# Revit family: 1_天吊埋込タイプ 標準 単相100V_3相200V-60
name_source: partatom
category: 機械設備
units: mm (PartAtom-declared; Revit-internal decimal feet)

## family parameters
OmniClass タイトル = Centrifugal Fans
OmniClass 番号 = 23.75.35.17.27
パーツ タイプ = 割り込み
ロード時にボイドで切り取り = いいえ
丸型コネクタ寸法 = 直径を使用
作業面ベース = いいえ
共有 = いいえ
常に垂直 = はい
部屋計算ポイント = はい

## types (18) — shared parameters
Clearance Left = 450  [stored 1.47638 ft]
IfcExportAs = IfcFanType
IfcExportType = CENTRIFUGALFORWARDCURVED
MID静圧 = 0.0 Pa
MID風量 = 0.0 m³/h
OmniClassCode = 23-33 31 19 13 15
URL = https://www.mitsubishielectric.co.jp
Uniclass2015Code = Pr_65_67_29_12
Uniclass2015Title = Centrifugal fans
Uniclass2015Version = Systems v1.9
サービススペース = はい
ファンの種類 = 多翼形
仕様書バージョン = Version1.0
企業コード = 108420
分類コード = 50052502100020
周波数 = 60 Hz
呼称 = 消音ボックス付送風機
実風量 = 0.0 m³/h
本体マテリアル = 溶融亜鉛めっき鋼板
極 = 4
法定耐用年数 = 15
盤工事区分 = 電気工事
積算_科目 = 2 換気設備
製品出荷対象 = 国内
製造元 = 三菱電機株式会社
設置方法 = 天吊
説明 = ストレートシロッコファン天吊埋込タイプ（標準形）
負荷分類 = 3_ファン類
運転質量 = 0.00 kg
zero-valued in all types: Clearance Back, Clearance Bottom, Clearance Front, Clearance Right, Clearance Top

## per-type parameters (varying)
- BFS-15SG: Depth=335  [stored 1.09908 ft]; Height=225  [stored 0.738189 ft]; M=100  [stored 0.328084 ft]; MAX静圧=39.0 Pa; MAX風量=150.0 m³/h; MIN静圧=26.0 Pa; MIN風量=96.0 m³/h; Width=223  [stored 0.731627 ft]; ダクト径=100 mm; 価格=30900 $; 天吊金具ピッチ奥行=300; 天吊金具ピッチ幅=299; 形名=BFS-SG : BFS-15SG; 極数=2; 消費電力=24 W; 番手=#1; 相=1; 製品リリース年月=2018年4月23日; 製品質量=6.00 kg; 質量=7.20 kg; 電動機出力=8 W; 電圧=100 V; 騒音レベル(dB(A))=34; 騒音レベル(dB(A))_側面=20; 騒音レベル(dB(A))_吐出=34; 騒音レベル(dB(A))_吸込=30
- BFS-30SG: Depth=335  [stored 1.09908 ft]; Height=225  [stored 0.738189 ft]; M=100  [stored 0.328084 ft]; MAX静圧=39.0 Pa; MAX風量=300.0 m³/h; MIN静圧=15.0 Pa; MIN風量=182.0 m³/h; Width=223  [stored 0.731627 ft]; ダクト径=150 mm; 価格=44700 $; 天吊金具ピッチ奥行=300; 天吊金具ピッチ幅=299; 形名=BFS-SG : BFS-30SG; 極数=2; 消費電力=44 W; 番手=#1; 相=1; 製品リリース年月=2018年4月23日; 製品質量=6.00 kg; 質量=7.20 kg; 電動機出力=16 W; 電圧=100 V; 騒音レベル(dB(A))=40; 騒音レベル(dB(A))_側面=23.5; 騒音レベル(dB(A))_吐出=40; 騒音レベル(dB(A))_吸込=36
- BFS-40SG: Depth=388  [stored 1.27297 ft]; Height=255  [stored 0.836614 ft]; M=100  [stored 0.328084 ft]; MAX静圧=59.0 Pa; MAX風量=400.0 m³/h; MIN静圧=30.0 Pa; MIN風量=273.0 m³/h; Width=255  [stored 0.836614 ft]; ダクト径=150 mm; 価格=52800 $; 天吊金具ピッチ奥行=353; 天吊金具ピッチ幅=331; 形名=BFS-SG : BFS-40SG; 極数=2; 消費電力=66 W; 番手=#1 1/4; 相=1; 製品リリース年月=2018年4月23日; 製品質量=8.00 kg; 質量=9.60 kg; 電動機出力=25 W; 電圧=100 V; 騒音レベル(dB(A))=44; 騒音レベル(dB(A))_側面=27; 騒音レベル(dB(A))_吐出=44; 騒音レベル(dB(A))_吸込=38
- BFS-50SG: Depth=423  [stored 1.3878 ft]; Height=255  [stored 0.836614 ft]; M=100  [stored 0.328084 ft]; MAX静圧=130.0 Pa; MAX風量=500.0 m³/h; MIN静圧=100.0 Pa; MIN風量=380.0 m³/h; Width=325  [stored 1.06627 ft]; ダクト径=200 mm; 価格=74800 $; 参照している仕様書等のバージョン=公共建築工事標準仕様書（機械設備工事編）平成31年度版; 天吊金具ピッチ奥行=388  [stored 1.27297 ft]; 天吊金具ピッチ幅=401; 形名=BFS-SG : BFS-50SG; 極数=2; 消費電力=88 W; 番手=#1 1/4; 相=1; 製品リリース年月=2018年4月23日; 製品質量=10.50 kg; 質量=12.60 kg; 電動機出力=45 W; 電圧=100 V; 騒音レベル(dB(A))=49; 騒音レベル(dB(A))_側面=25.5; 騒音レベル(dB(A))_吐出=49; 騒音レベル(dB(A))_吸込=37.5
- BFS-65SG: Depth=488  [stored 1.60105 ft]; Height=305  [stored 1.00066 ft]; M=100  [stored 0.328084 ft]; MAX静圧=118.0 Pa; MAX風量=650.0 m³/h; MIN静圧=91.0 Pa; MIN風量=498.0 m³/h; Width=373  [stored 1.22375 ft]; ダクト径=200 mm; 価格=79400 $; 参照している仕様書等のバージョン=公共建築工事標準仕様書（機械設備工事編）平成31年度版; 天吊金具ピッチ奥行=453  [stored 1.48622 ft]; 天吊金具ピッチ幅=449  [stored 1.4731 ft]; 形名=BFS-SG : BFS-65SG; 極数=2; 消費電力=126 W; 番手=#1 1/4; 相=1; 製品リリース年月=2018年4月23日; 製品質量=13.00 kg; 質量=15.60 kg; 電動機出力=65 W; 電圧=100 V; 騒音レベル(dB(A))=51; 騒音レベル(dB(A))_側面=29; 騒音レベル(dB(A))_吐出=51; 騒音レベル(dB(A))_吸込=38
- BFS-80SG: Depth=488  [stored 1.60105 ft]; Height=305  [stored 1.00066 ft]; M=100  [stored 0.328084 ft]; MAX静圧=98.0 Pa; MAX風量=800.0 m³/h; MIN静圧=88.0 Pa; MIN風量=600.0 m³/h; Width=373  [stored 1.22375 ft]; ダクト径=200 mm; 価格=83900 $; 参照している仕様書等のバージョン=公共建築工事標準仕様書（機械設備工事編）平成31年度版; 天吊金具ピッチ奥行=453  [stored 1.48622 ft]; 天吊金具ピッチ幅=449  [stored 1.4731 ft]; 形名=BFS-SG : BFS-80SG; 極数=2; 消費電力=155 W; 番手=#1 1/4; 相=1; 製品リリース年月=2018年4月23日; 製品質量=13.50 kg; 質量=16.20 kg; 電動機出力=80 W; 電圧=100 V; 騒音レベル(dB(A))=53; 騒音レベル(dB(A))_側面=30.5; 騒音レベル(dB(A))_吐出=53; 騒音レベル(dB(A))_吸込=39.5
- BFS-90SG: Depth=488  [stored 1.60105 ft]; Height=305  [stored 1.00066 ft]; M=100  [stored 0.328084 ft]; MAX静圧=128.0 Pa; MAX風量=900.0 m³/h; MIN静圧=110.0 Pa; MIN風量=684.0 m³/h; Width=393  [stored 1.28937 ft]; ダクト径=200 mm; 価格=88500 $; 参照している仕様書等のバージョン=公共建築工事標準仕様書（機械設備工事編）平成31年度版; 天吊金具ピッチ奥行=453  [stored 1.48622 ft]; 天吊金具ピッチ幅=469; 形名=BFS-SG : BFS-90SG; 極数=2; 消費電力=205 W; 番手=#1 1/2; 相=1; 製品リリース年月=2018年4月23日; 製品質量=15.50 kg; 質量=18.60 kg; 電動機出力=110 W; 電圧=100 V; 騒音レベル(dB(A))=55; 騒音レベル(dB(A))_側面=32; 騒音レベル(dB(A))_吐出=55; 騒音レベル(dB(A))_吸込=41
- BFS-100SG: Depth=488  [stored 1.60105 ft]; Height=305  [stored 1.00066 ft]; M=100  [stored 0.328084 ft]; MAX静圧=145.0 Pa; MAX風量=1000.0 m³/h; MIN静圧=187.0 Pa; MIN風量=865.0 m³/h; Width=393  [stored 1.28937 ft]; ダクト径=200 mm; 価格=93600 $; 参照している仕様書等のバージョン=公共建築工事標準仕様書（機械設備工事編）平成31年度版; 天吊金具ピッチ奥行=453  [stored 1.48622 ft]; 天吊金具ピッチ幅=469; 形名=BFS-SG : BFS-100SG; 極数=2; 消費電力=247 W; 番手=#1 1/2; 相=1; 製品リリース年月=2018年4月23日; 製品質量=16.00 kg; 質量=19.20 kg; 電動機出力=160 W; 電圧=100 V; 騒音レベル(dB(A))=58; 騒音レベル(dB(A))_側面=34.5; 騒音レベル(dB(A))_吐出=58; 騒音レベル(dB(A))_吸込=43
- BFS-120SG: Depth=590  [stored 1.9357 ft]; Height=350  [stored 1.14829 ft]; M=100  [stored 0.328084 ft]; MAX静圧=220.0 Pa; MAX風量=1200.0 m³/h; MIN静圧=195.0 Pa; MIN風量=1030.0 m³/h; Width=391; ダクト径=250 mm; 価格=102100 $; 参照している仕様書等のバージョン=公共建築工事標準仕様書（機械設備工事編）平成31年度版; 天吊金具ピッチ奥行=555  [stored 1.82087 ft]; 天吊金具ピッチ幅=467  [stored 1.53215 ft]; 形名=BFS-SG : BFS-120SG; 極数=2; 消費電力=352 W; 番手=#1 1/2; 相=1; 製品リリース年月=2018年4月23日; 製品質量=19.50 kg; 質量=23.40 kg; 電動機出力=200 W; 電圧=100 V; 騒音レベル(dB(A))=59; 騒音レベル(dB(A))_側面=34.5; 騒音レベル(dB(A))_吐出=59; 騒音レベル(dB(A))_吸込=46.5
- BFS-150SG: Depth=590  [stored 1.9357 ft]; Height=350  [stored 1.14829 ft]; M=100  [stored 0.328084 ft]; MAX静圧=180.0 Pa; MAX風量=1500.0 m³/h; MIN静圧=184.0 Pa; MIN風量=1243.0 m³/h; Width=391; ダクト径=250 mm; 価格=108200 $; 参照している仕様書等のバージョン=公共建築工事標準仕様書（機械設備工事編）平成31年度版; 天吊金具ピッチ奥行=555  [stored 1.82087 ft]; 天吊金具ピッチ幅=467  [stored 1.53215 ft]; 形名=BFS-SG : BFS-150SG; 極数=2; 消費電力=498 W; 番手=#1 1/2; 相=1; 製品リリース年月=2018年4月23日; 製品質量=19.50 kg; 質量=23.40 kg; 電動機出力=340 W; 電圧=100 V; 騒音レベル(dB(A))=63; 騒音レベル(dB(A))_側面=37.5; 騒音レベル(dB(A))_吐出=63; 騒音レベル(dB(A))_吸込=50
- BFS-180TG: Depth=645  [stored 2.11614 ft]; Height=350  [stored 1.14829 ft]; M=85  [stored 0.278871 ft]; MAX静圧=167.0 Pa; MAX風量=1800.0 m³/h; MIN静圧=0.0 Pa; MIN風量=0.0 m³/h; Width=476  [stored 1.56168 ft]; ダクト径=250 mm; 価格=123900 $; 参照している仕様書等のバージョン=公共建築工事標準仕様書（機械設備工事編）平成31年度版; 天吊金具ピッチ奥行=610  [stored 2.00131 ft]; 天吊金具ピッチ幅=552  [stored 1.81102 ft]; 形名=BFS-TG : BFS-180TG; 極数=3; 消費電力=573 W; 番手=#1 1/2; 相=3; 製品リリース年月=2018年4月23日; 製品質量=22.50 kg; 質量=27.00 kg; 電動機出力=360 W; 電圧=200 V; 騒音レベル(dB(A))=64; 騒音レベル(dB(A))_側面=38.5; 騒音レベル(dB(A))_吐出=64; 騒音レベル(dB(A))_吸込=50
- BFS-210TG: Depth=645  [stored 2.11614 ft]; Height=350  [stored 1.14829 ft]; M=100  [stored 0.328084 ft]; MAX静圧=191.0 Pa; MAX風量=2100.0 m³/h; MIN静圧=0.0 Pa; MIN風量=0.0 m³/h; Width=476  [stored 1.56168 ft]; ダクト径=300 mm; 価格=176400 $; 参照している仕様書等のバージョン=公共建築工事標準仕様書（機械設備工事編）平成31年度版; 天吊金具ピッチ奥行=610  [stored 2.00131 ft]; 天吊金具ピッチ幅=552  [stored 1.81102 ft]; 形名=BFS-TG : BFS-210TG; 極数=3; 消費電力=665 W; 番手=#1 1/2; 相=3; 製品リリース年月=2018年4月23日; 製品質量=22.50 kg; 質量=27.00 kg; 電動機出力=490 W; 電圧=200 V; 騒音レベル(dB(A))=67; 騒音レベル(dB(A))_側面=40; 騒音レベル(dB(A))_吐出=67; 騒音レベル(dB(A))_吸込=52.5
- BFS-240TA: Depth=717  [stored 2.35236 ft]; Height=373  [stored 1.22375 ft]; M=100  [stored 0.328084 ft]; MAX静圧=220.0 Pa; MAX風量=2400.0 m³/h; MIN静圧=0.0 Pa; MIN風量=0.0 m³/h; Width=493  [stored 1.61745 ft]; ダクト径=300 mm; 価格=182000 $; 参照している仕様書等のバージョン=公共建築工事標準仕様書（機械設備工事編）平成31年度版; 天吊金具ピッチ奥行=664  [stored 2.17848 ft]; 天吊金具ピッチ幅=602  [stored 1.97507 ft]; 形名=BFS-TG : BFS-240TA; 極数=3; 消費電力=810 W; 番手=#1 1/2; 相=3; 製品リリース年月=2003年4月; 製品質量=33.00 kg; 質量=39.60 kg; 電動機出力=1100 W; 電圧=200 V; 騒音レベル(dB(A))=69; 騒音レベル(dB(A))_側面=42.5; 騒音レベル(dB(A))_吐出=69; 騒音レベル(dB(A))_吸込=51.5
- BFS-80TG: Depth=488  [stored 1.60105 ft]; Height=305  [stored 1.00066 ft]; M=85  [stored 0.278871 ft]; MAX静圧=98.0 Pa; MAX風量=800.0 m³/h; MIN静圧=73.0 Pa; MIN風量=550.0 m³/h; Width=373  [stored 1.22375 ft]; ダクト径=200 mm; 価格=83900 $; 参照している仕様書等のバージョン=公共建築工事標準仕様書（機械設備工事編）平成31年度版; 天吊金具ピッチ奥行=453  [stored 1.48622 ft]; 天吊金具ピッチ幅=449  [stored 1.4731 ft]; 形名=BFS-TG : BFS-80TG; 極数=3; 消費電力=148 W; 番手=#1 1/4; 相=3; 製品リリース年月=2018年4月23日; 製品質量=15.00 kg; 質量=18.00 kg; 電動機出力=80 W; 電圧=200 V; 騒音レベル(dB(A))=53; 騒音レベル(dB(A))_側面=31.5; 騒音レベル(dB(A))_吐出=53; 騒音レベル(dB(A))_吸込=40
- BFS-90TG: Depth=488  [stored 1.60105 ft]; Height=305  [stored 1.00066 ft]; M=85  [stored 0.278871 ft]; MAX静圧=128.0 Pa; MAX風量=900.0 m³/h; MIN静圧=96.0 Pa; MIN風量=640.0 m³/h; Width=393  [stored 1.28937 ft]; ダクト径=200 mm; 価格=88500 $; 参照している仕様書等のバージョン=公共建築工事標準仕様書（機械設備工事編）平成31年度版; 天吊金具ピッチ奥行=453  [stored 1.48622 ft]; 天吊金具ピッチ幅=469; 形名=BFS-TG : BFS-90TG; 極数=3; 消費電力=194 W; 番手=#1 1/2; 相=3; 製品リリース年月=2018年4月23日; 製品質量=15.50 kg; 質量=18.60 kg; 電動機出力=100 W; 電圧=200 V; 騒音レベル(dB(A))=55; 騒音レベル(dB(A))_側面=34; 騒音レベル(dB(A))_吐出=55; 騒音レベル(dB(A))_吸込=41
- BFS-100TG: Depth=488  [stored 1.60105 ft]; Height=305  [stored 1.00066 ft]; M=85  [stored 0.278871 ft]; MAX静圧=145.0 Pa; MAX風量=1000.0 m³/h; MIN静圧=115.0 Pa; MIN風量=678.0 m³/h; Width=393  [stored 1.28937 ft]; ダクト径=200 mm; 価格=93600 $; 参照している仕様書等のバージョン=公共建築工事標準仕様書（機械設備工事編）平成31年度版; 天吊金具ピッチ奥行=453  [stored 1.48622 ft]; 天吊金具ピッチ幅=469; 形名=BFS-TG : BFS-100TG; 極数=3; 消費電力=237 W; 番手=#1 1/2; 相=3; 製品リリース年月=2018年4月23日; 製品質量=15.50 kg; 質量=18.60 kg; 電動機出力=150 W; 電圧=200 V; 騒音レベル(dB(A))=58; 騒音レベル(dB(A))_側面=34; 騒音レベル(dB(A))_吐出=58; 騒音レベル(dB(A))_吸込=43
- BFS-120TG: Depth=590  [stored 1.9357 ft]; Height=350  [stored 1.14829 ft]; M=85  [stored 0.278871 ft]; MAX静圧=220.0 Pa; MAX風量=1200.0 m³/h; MIN静圧=121.0 Pa; MIN風量=821.0 m³/h; Width=391; ダクト径=250 mm; 価格=102100 $; 参照している仕様書等のバージョン=公共建築工事標準仕様書（機械設備工事編）平成31年度版; 天吊金具ピッチ奥行=555  [stored 1.82087 ft]; 天吊金具ピッチ幅=467  [stored 1.53215 ft]; 形名=BFS-TG : BFS-120TG; 極数=3; 消費電力=342 W; 番手=#1 1/2; 相=3; 製品リリース年月=2018年4月23日; 製品質量=19.50 kg; 質量=23.40 kg; 電動機出力=180 W; 電圧=200 V; 騒音レベル(dB(A))=58; 騒音レベル(dB(A))_側面=35.5; 騒音レベル(dB(A))_吐出=58; 騒音レベル(dB(A))_吸込=46.5
- BFS-150TG: Depth=590  [stored 1.9357 ft]; Height=350  [stored 1.14829 ft]; M=85  [stored 0.278871 ft]; MAX静圧=180.0 Pa; MAX風量=1500.0 m³/h; MIN静圧=132.0 Pa; MIN風量=1057.0 m³/h; Width=391; ダクト径=250 mm; 価格=108200 $; 参照している仕様書等のバージョン=公共建築工事標準仕様書（機械設備工事編）平成31年度版; 天吊金具ピッチ奥行=555  [stored 1.82087 ft]; 天吊金具ピッチ幅=467  [stored 1.53215 ft]; 形名=BFS-TG : BFS-150TG; 極数=3; 消費電力=440 W; 番手=#1 1/2; 相=3; 製品リリース年月=2018年4月23日; 製品質量=20.00 kg; 質量=24.00 kg; 電動機出力=280 W; 電圧=200 V; 騒音レベル(dB(A))=63; 騒音レベル(dB(A))_側面=37.5; 騒音レベル(dB(A))_吐出=63; 騒音レベル(dB(A))_吸込=50

note: column(s) folded — value = type name in every type: モデル

note: [stored X ft] marks values corroborated as IEEE doubles in the binary element streams (Revit-internal decimal feet)
